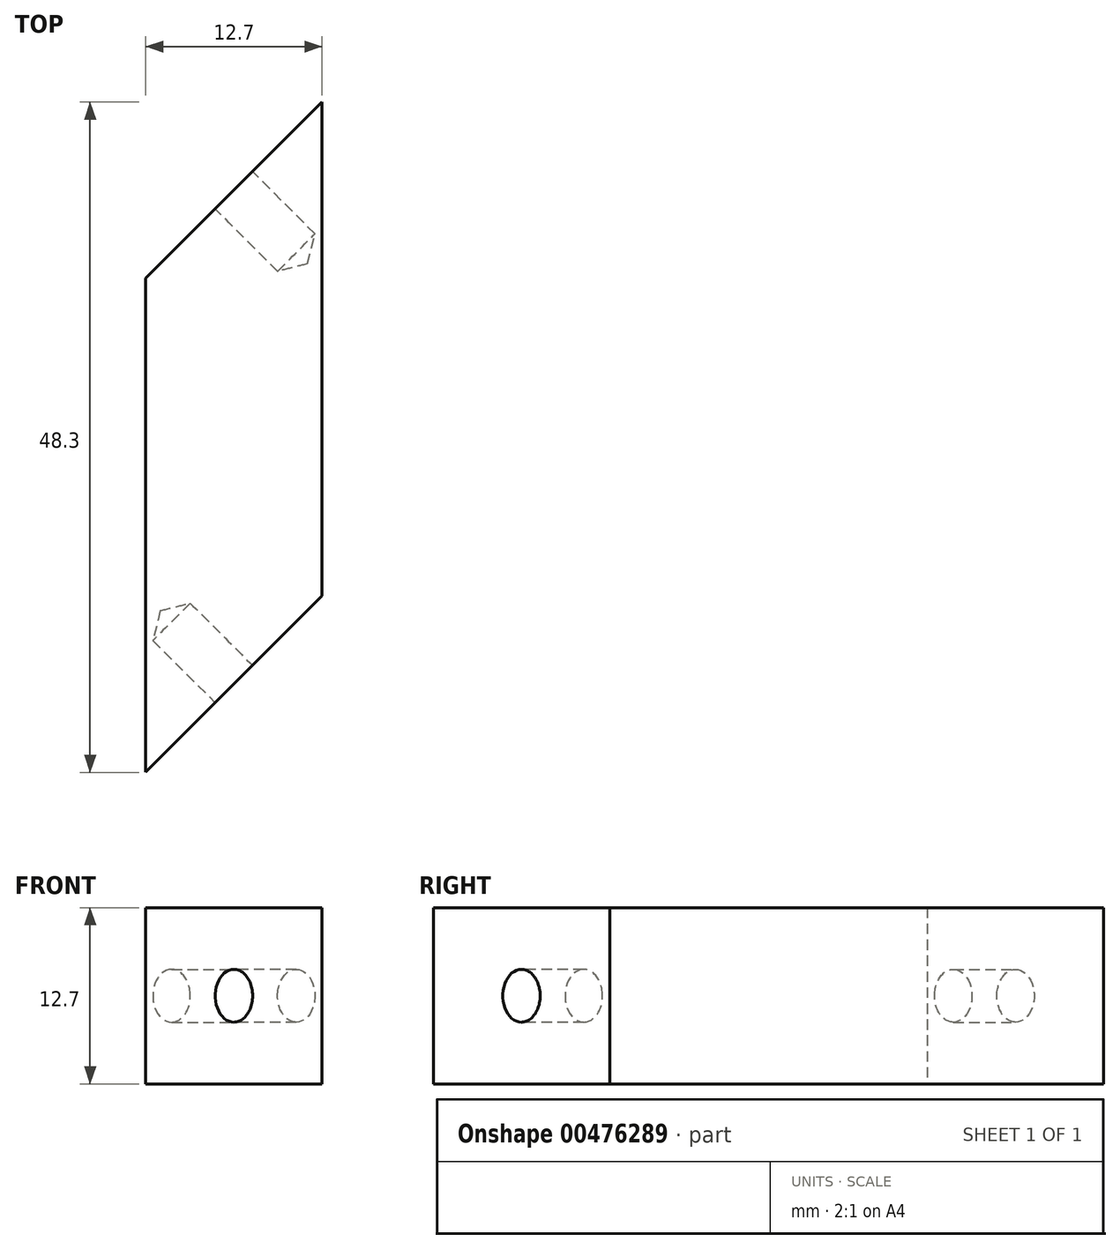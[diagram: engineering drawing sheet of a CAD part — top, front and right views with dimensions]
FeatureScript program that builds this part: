
annotation { "Feature Type Name" : "Feature", "Feature Type Description" : "" }
export const myFeature = defineFeature(function(context is Context, id is Id, definition is map)
    precondition{}
    {
        {
            var Q0;
            Q0=qCreatedBy(makeId("Top.planeOp"),FACE);
            var sketch = newSketch(context, id + "F0", { "sketchPlane" : qUnion([Q0])});
            skLineSegment(sketch, "E0.bottom", {"start": v(7.69, 24.15) * mm, "end": v(-5.01, 24.15) * mm});
            skLineSegment(sketch, "E0.top", {"start": v(7.69, -24.15) * mm, "end": v(-5.01, -24.15) * mm});
            skLineSegment(sketch, "E0.left", {"start": v(7.69, 24.15) * mm, "end": v(7.69, -24.15) * mm});
            skLineSegment(sketch, "E0.right", {"start": v(-5.01, 24.15) * mm, "end": v(-5.01, -24.15) * mm});
            skPoint(sketch, "E0.middle", {"position": v(1.34, 0) * mm});
            skSolve(sketch);
        }
        {
            var Q0;
            Q0=makeQuery(id+"F0.imprint","IMPRINT",FACE,{"disambiguationData":[TD([[makeQuery(id+"F0.imprint","IMPRINT",EDGE,{"derivedFrom":sQuery(id+"F0.wireOp",EDGE,"E0.bottom")}),1.0]])]});
            extrude(context, id + "F1", {"entities" : qUnion([Q0]), "depth" : 12.7 * mm});
        }
        {
            var Q0;
            Q0=makeQuery(id+"F1.opExtrude","SWEPT_EDGE",EDGE,{"disambiguationData":[OSD([sQuery(id+"F0.wireOp",EDGE,"E0.top"),sQuery(id+"F0.wireOp",EDGE,"E0.left")])]});
            chamfer(context, id + "F2", {"entities" : qUnion([Q0]), "chamferType" : ChamferType.TWO_OFFSETS, "width1" : 12.7 * mm, "oppositeDirection" : false, "width2" : 12.7 * mm, "tangentPropagation" : true});
        }
        {
            var Q0;
            Q0=makeQuery(id+"F1.opExtrude","SWEPT_EDGE",EDGE,{"disambiguationData":[OSD([sQuery(id+"F0.wireOp",EDGE,"E0.bottom"),sQuery(id+"F0.wireOp",EDGE,"E0.right")])]});
            chamfer(context, id + "F3", {"entities" : qUnion([Q0]), "chamferType" : ChamferType.TWO_OFFSETS, "width1" : 12.7 * mm, "oppositeDirection" : false, "width2" : 12.7 * mm, "tangentPropagation" : true});
        }
        {
            var Q0;
            Q0=makeQuery(id+"F3.opChamfer","BLEND_FACE",FACE,{"disambiguationData":[OSD([sQuery(id+"F0.wireOp",EDGE,"E0.bottom"),sQuery(id+"F0.wireOp",EDGE,"E0.right")])]});
            var sketch = newSketch(context, id + "F4", { "sketchPlane" : qUnion([Q0])});
            skCircle(sketch, "E1", {"center": v(-13.53, 6.35) * mm, "radius": 1.9 * mm});
            skSolve(sketch);
        }
        {
            var Q0;
            Q0=makeQuery(id+"F2.opChamfer","BLEND_FACE",FACE,{"disambiguationData":[OSD([sQuery(id+"F0.wireOp",EDGE,"E0.top"),sQuery(id+"F0.wireOp",EDGE,"E0.left")])]});
            var sketch = newSketch(context, id + "F5", { "sketchPlane" : qUnion([Q0])});
            skCircle(sketch, "E2", {"center": v(-11.64, 6.35) * mm, "radius": 1.9 * mm});
            skSolve(sketch);
        }
        {
            var Q0;
            Q0=sQuery(id+"F5.wireOp",VERTEX,"E2.center");
            var Q1;
            Q1=sQuery(id+"F4.wireOp",VERTEX,"E1.center");
            var Q2;
            Q2=makeQuery(id+"F1.opExtrude","SWEPT_BODY",BODY,{"disambiguationData":[OSD([sQuery(id+"F0.wireOp",EDGE,"E0.bottom"),sQuery(id+"F0.wireOp",EDGE,"E0.top"),sQuery(id+"F0.wireOp",EDGE,"E0.left"),sQuery(id+"F0.wireOp",EDGE,"E0.right")])]});
            hole(context, id + "F6", {"style" : HoleStyle.SIMPLE, "endStyle" : HoleEndStyle.BLIND, "holeDiameter" : 3.8 * mm, "holeDepth" : 6.35 * mm, "isTappedThrough" : true, "tappedDepth" : 12.7 * mm, "tapClearance" : 3, "locations" : qUnion([Q0, Q1]), "scope" : qUnion([Q2])});
        }
    });
